# Revit family: pefy-p45_160mg9-j_60Hz
name_source: partatom
category: 機械設備
units: mm (PartAtom-declared; Revit-internal decimal feet)

## family parameters
OmniClass タイトル = Split System Air Conditioning Units
OmniClass 番号 = 23.75.10.24.21.27.27
パーツ タイプ = 標準
ロード時にボイドで切り取り = いいえ
丸型コネクタ寸法 = 直径を使用
作業面ベース = いいえ
共有 = いいえ
常に垂直 = はい
部屋計算ポイント = はい

## types (8) — shared parameters
Clearance Back = 50  [stored 0.164042 ft]
Clearance Bottom = 20  [stored 0.0656168 ft]
Clearance Front = 575
Clearance Right = 50  [stored 0.164042 ft]
Clearance Top = 20  [stored 0.0656168 ft]
Depth = 900  [stored 2.95276 ft]
Height = 380  [stored 1.24672 ft]
IfcExportAs = IfcUnitaryEquipmentType
IfcExportType = AIRCONDITIONINGUNIT
OmniClassCode = 23-751024212727
RAサイズ_D = 340  [stored 1.11549 ft]
SAサイズ_D = 250  [stored 0.82021 ft]
S_H = 400  [stored 1.31234 ft]
URL = https://www.mitsubishielectric.co.jp
Uniclass2015Code = Pr_70_65_03_84
Uniclass2015Title = Split coil remote air cooled condensing units
Uniclass2015Version = Systems v1.9
ケーブルサイズ = 2 mm
サービススペース = はい
ドレン管_横 = 430
ドレン管_縦 = 326.5  [stored 1.07119 ft]
ドレン管径 = 32 mm
仕様書バージョン = Version1.0
企業コード = 108420
冷媒ガス管_横 = 187  [stored 0.613517 ft]
冷媒ガス管_縦 = 143
冷媒液管_横 = 69  [stored 0.226378 ft]
冷媒液管_縦 = 58  [stored 0.190289 ft]
冷媒管径 = 100 mm
冷媒高低圧ガス管径 = 0 mm
分類コード = 50053003221070
加湿給水管径 = 0 mm
参照している仕様書等のバージョン = 公共建築工事標準仕様書（機械設備工事編）平成31年度版
吊り位置Y = 842  [stored 2.76247 ft]
吊り幅 = 60  [stored 0.19685 ft]
周波数 = 60 Hz
呼称 = 室内機_天井吊(隠ぺい)形(両ダクト形)
形式 = 天井吊（隠ぺい）形（両ダクト形）
推奨ブレーカー容量 = 15 A
本体マテリアル = <カテゴリ別>
極数 = 3
機外静圧 = 100.0 Pa
法定耐用年数 = 15
消費電力_加湿器 = 0.00 kW
消費電力_電気ヒーター = 0.00 kW
点検口 = はい
点検口位置 = 100  [stored 0.328084 ft]
点検口設置範囲 = 700  [stored 2.29659 ft]
発停方法 = 付属スイッチ
相 = 1
相_電気ヒーター = 1
積算_科目 = 1 空気調和設備
符号 = ACP_CID
製品リリース年月 = 2022年9月15日
製品出荷対象 = 国内
製造元 = 三菱電機株式会社
設置方法 = 天井吊(隠ぺい)形
設計冷房能力 = 0 kW
設計冷房能力_顕熱 = 0 kW
設計暖房能力 = 0.00 kW
説明 = ビル用マルチエアコン 天井埋込形　室内機
負荷分類 = 3_ファン類
運転質量 = 0.00 kg
電圧 = 200 V
電圧_電気ヒーター = 0 V
zero-valued in all types: 有効加湿量, 電源_H

## per-type parameters (varying)
| type | Clearance Left | MAX風量 | MIN風量 | RAサイズ_W | SAサイズ_W | Width | 冷媒ガス管径 | 冷媒液管径 | 冷媒管径符号 | 冷房能力 | 吊り位置X | 暖房能力 | 消費電力 | 消費電力_冷房 | 消費電力_暖房 | 製品質量 | 質量 | 電動機出力_送風機 | 音響パワーレベル(dB) | 音響パワーレベル（弱）(dB) | 風量 | 風量（m3／min） | 風量（弱）（m3／min） |
| PEFY-P45MG9-J | 730  [stored 2.39501 ft] | 840.0 m³/h | 600.0 m³/h | 600 | 550  [stored 1.80446 ft] | 745  [stored 2.44423 ft] | 13 mm | 6 mm | Ac | 4.5 kW | 754  [stored 2.47375 ft] | 5.00 kW | 0.22 kW | 0.22 kW | 0.20 kW | 39.00 kg | 46.80 kg | 0.08 kW | 57 | 51 | 840.0 m³/h | 14 | 10 |
| PEFY-P56MG9-J | 730  [stored 2.39501 ft] | 840.0 m³/h | 600.0 m³/h | 600 | 550  [stored 1.80446 ft] | 745  [stored 2.44423 ft] | 13 mm | 6 mm | Ac | 5.6 kW | 754  [stored 2.47375 ft] | 6.30 kW | 0.22 kW | 0.22 kW | 0.20 kW | 39.00 kg | 46.80 kg | 0.08 kW | 57 | 52 | 840.0 m³/h | 14 | 10 |
| PEFY-P71MG9-J | 730  [stored 2.39501 ft] | 1140.0 m³/h | 810.0 m³/h | 600 | 550  [stored 1.80446 ft] | 745  [stored 2.44423 ft] | 16 mm | 10 mm | Bd | 7.1 kW | 754  [stored 2.47375 ft] | 8.00 kW | 0.28 kW | 0.28 kW | 0.26 kW | 40.00 kg | 48.00 kg | 0.10 kW | 61 | 56 | 1140.0 m³/h | 19 | 13.5 |
| PEFY-P80MG9-J | 1015  [stored 3.33005 ft] | 1320.0 m³/h | 930.0 m³/h | 885 | 835 | 1030  [stored 3.37927 ft] | 16 mm | 10 mm | Bd | 8 kW | 1039  [stored 3.40879 ft] | 9.00 kW | 0.31 kW | 0.31 kW | 0.29 kW | 51.00 kg | 61.20 kg | 0.11 kW | 61 | 56 | 1320.0 m³/h | 22 | 15.5 |
| PEFY-P90MG9-J | 1015  [stored 3.33005 ft] | 1500.0 m³/h | 1080.0 m³/h | 885 | 835 | 1030  [stored 3.37927 ft] | 16 mm | 10 mm | Bd | 9 kW | 1039  [stored 3.40879 ft] | 10.00 kW | 0.33 kW | 0.33 kW | 0.31 kW | 51.00 kg | 61.20 kg | 0.14 kW | 63 | 58 | 1500.0 m³/h | 25 | 18 |
| PEFY-P112MG9-J | 1180  [stored 3.87139 ft] | 2280.0 m³/h | 1590.0 m³/h | 1050 | 1000  [stored 3.28084 ft] | 1195  [stored 3.9206 ft] | 16 mm | 10 mm | Bd | 11.2 kW | 1204  [stored 3.95013 ft] | 12.50 kW | 0.55 kW | 0.55 kW | 0.53 kW | 63.00 kg | 75.60 kg | 0.20 kW | 64 | 60 | 2280.0 m³/h | 38 | 26.5 |
| PEFY-P140MG9-J | 1180  [stored 3.87139 ft] | 2280.0 m³/h | 1590.0 m³/h | 1050 | 1000  [stored 3.28084 ft] | 1195  [stored 3.9206 ft] | 16 mm | 10 mm | Bd | 14 kW | 1204  [stored 3.95013 ft] | 16.00 kW | 0.55 kW | 0.55 kW | 0.53 kW | 63.00 kg | 75.60 kg | 0.20 kW | 65 | 61 | 2280.0 m³/h | 38 | 26.5 |
| PEFY-P160MG9-J | 1180  [stored 3.87139 ft] | 2400.0 m³/h | 1680.0 m³/h | 1050 | 1000  [stored 3.28084 ft] | 1195  [stored 3.9206 ft] | 16 mm | 10 mm | Bd | 16 kW | 1204  [stored 3.95013 ft] | 18.00 kW | 0.55 kW | 0.55 kW | 0.53 kW | 65.00 kg | 78.00 kg | 0.23 kW | 65 | 62 | 2400.0 m³/h | 40 | 28 |

note: column(s) folded — value = type name in every type: モデル

note: [stored X ft] marks values corroborated as IEEE doubles in the binary element streams (Revit-internal decimal feet)

## geometry (parser evidence)
native form markers: Blend x4
no freeform markers — native parametric forms only
